# Revit family: Shower_Head-Ceiling_Mount-Grohe-Rainshower_F_Series_9-26869000
name_source: partatom
category: Plumbing Fixtures
units: mm (PartAtom-declared; Revit-internal decimal feet)

## family parameters
Always vertical = No
Cut with Voids When Loaded = No
OmniClass Number = 23.45.05.14.17
OmniClass Title = Showers
Part Type = Normal
Room Calculation Point = No
Round Connector Dimension = Use Diameter
Shared = Yes
Work Plane-Based = Yes

## types (1)
- 26869000
    ASME A112.18.1/CSA B125.1 = Yes
    Assembly Code = D2010710
    CEC Compliant = Yes
    CW Connection = No
    CWFU = 3
    CalGreen Compliant = Yes
    Default Elevation = 0"
    Description = Rainshower 230 Ceiling Shower Head, 9" 1 Spray 1.75 gpm
    Finish = Metal-Grohe-000-StarLight Chrome
    Flow Rate = 1.75gpm (6.6L/min)
    GROHE DreamSpray = Yes
    GROHE DripStop = Yes
    GROHE EcoJoy = Yes
    GROHE StarLight = Yes
    HW Connection = No
    HWFU = 3
    Height = 1/2"
    Installation Type = Ceiling Mounted
    Manufacturer = Grohe
    Material = Metal-Grohe-000-StarLight Chrome
    Model = 26869000
    Price = Prices may vary. Please consult Manufacturer Representative for most up-to-date price list.
    Speed Clean = Yes
    Tempered Connection Diameter = 1/2"
    Tempered Connection Radius = 1/4"
    Tempered Water Connection = Yes
    URL = https://www.grohe.ca
    Vent Connection = No
    WFU = 4
    Waste Connection = No
    WaterSense = Yes
    Width = 9 1/16"
    cUPC Compliant = Yes

## geometry (parser evidence)
native form markers: Sweep x2
no freeform markers — native parametric forms only
